FCSTD DOCUMENT  (FreeCAD 0.19R16699 (Git))
Label: RD701F Series
License: All rights reserved
LicenseURL: http://en.wikipedia.org/wiki/All_rights_reserved
objects: Sketcher::SketchObject×1, PartDesign::Body×1
note: 2 computed .brp shape members not serialized (recipe doc carries the construction recipe); baked Part::Feature solids carry a one-line shape summary decoded from their .brp

FEATURE [Sketcher::SketchObject] Sketch  label="MasterSketch"
  MapMode = 5
  Support = -> [XY_Plane]
  expr: Constraints[65] = MasterSketch.Constraints.antirotationtabdepth
  expr: Constraints.bodydepthtotal = MasterSketch.Constraints.bodyreardepth + MasterSketch.Constraints.bodyfrontdepth
  sketch-geometry (26):
    g0: LineSegment StartX=-3.85 StartY=3.85 StartZ=0 EndX=3.85 EndY=3.85 EndZ=0
    g1: LineSegment StartX=3.85 StartY=3.85 StartZ=0 EndX=3.85 EndY=-5.5 EndZ=0
    g2: LineSegment StartX=3.85 StartY=-5.5 StartZ=0 EndX=-3.85 EndY=-5.5 EndZ=0
    g3: LineSegment StartX=-3.85 StartY=-5.5 StartZ=0 EndX=-3.85 EndY=3.85 EndZ=0
    g4: GeomPoint X=-3.85 Y=0 Z=0
    g5: GeomPoint X=3.85 Y=0 Z=0
    g6: LineSegment StartX=-13.2904 StartY=12.005 StartZ=0 EndX=-14.7904 EndY=12.005 EndZ=0
    g7: LineSegment StartX=-14.7904 StartY=12.005 StartZ=0 EndX=-14.7904 EndY=2.65497 EndZ=0
    g8: LineSegment StartX=-14.7904 StartY=2.65497 StartZ=0 EndX=-13.2904 EndY=2.65497 EndZ=0
    g9: LineSegment StartX=-13.2904 StartY=2.65497 StartZ=0 EndX=-13.2904 EndY=12.005 EndZ=0
    g10: LineSegment StartX=-14.7904 StartY=2.65497 StartZ=0 EndX=-17.7904 EndY=2.65497 EndZ=0
    g11: LineSegment StartX=-17.7904 StartY=2.65497 StartZ=0 EndX=-17.7904 EndY=12.005 EndZ=0
    g12: LineSegment StartX=-17.7904 StartY=12.005 StartZ=0 EndX=-14.7904 EndY=12.005 EndZ=0
    g13: LineSegment StartX=-14.7904 StartY=12.005 StartZ=0 EndX=-14.7904 EndY=2.65497 EndZ=0
    g14: LineSegment StartX=-17.7904 StartY=12.005 StartZ=0 EndX=-18.5904 EndY=12.005 EndZ=0
    g15: LineSegment StartX=-18.5904 StartY=12.005 StartZ=0 EndX=-18.5904 EndY=2.65497 EndZ=0
    g16: LineSegment StartX=-18.5904 StartY=2.65497 StartZ=0 EndX=-17.7904 EndY=2.65497 EndZ=0
    g17: LineSegment StartX=-17.7904 StartY=2.65497 StartZ=0 EndX=-17.7904 EndY=12.005 EndZ=0
    g18: LineSegment StartX=-18.5904 StartY=2.65497 StartZ=0 EndX=-19.3904 EndY=2.65497 EndZ=0
    g19: LineSegment StartX=-19.3904 StartY=2.65497 StartZ=0 EndX=-19.3904 EndY=3.45497 EndZ=0
    g20: LineSegment StartX=-19.3904 StartY=3.45497 StartZ=0 EndX=-18.5904 EndY=3.45497 EndZ=0
    g21: LineSegment StartX=-18.5904 StartY=3.45497 StartZ=0 EndX=-18.5904 EndY=2.65497 EndZ=0
    g22: LineSegment StartX=-1 StartY=-5.5 StartZ=0 EndX=1 EndY=-5.5 EndZ=0
    g23: LineSegment StartX=1 StartY=-5.5 StartZ=0 EndX=1 EndY=-4.7 EndZ=0
    g24: LineSegment StartX=1 StartY=-4.7 StartZ=0 EndX=-1 EndY=-4.7 EndZ=0
    g25: LineSegment StartX=-1 StartY=-4.7 StartZ=0 EndX=-1 EndY=-5.5 EndZ=0
  constraints (67):
    c: Coincident(g0,g1)
    c: Coincident(g1,g2)
    c: Coincident(g2,g3)
    c: Coincident(g3,g0)
    c: Horizontal(g2)
    c: Vertical(g1)
    c: Vertical(g3)
    c: PointOnObject(g4,g3)
    c: PointOnObject(g5,g1)
    c: PointOnObject(g5,g-1)
    c: PointOnObject(g4,g-1)
    c: DistanceY(g5,g0) = 3.85  'bodyreardepth'
    c: DistanceY(g1,g5) = 5.5  'bodyfrontdepth'
    c: DistanceX(g0,g0) = 7.7  'bodywidth'
    c: Symmetric(g0,g0,g-2)
    c: Coincident(g6,g7)
    c: Coincident(g7,g8)
    c: Coincident(g8,g9)
    c: Coincident(g9,g6)
    c: Horizontal(g6)
    c: Horizontal(g8)
    c: Vertical(g7)
    c: Vertical(g9)
    c: Coincident(g10,g11)
    c: Coincident(g11,g12)
    c: Coincident(g12,g13)
    c: Coincident(g13,g10)
    c: Horizontal(g10)
    c: Horizontal(g12)
    c: Vertical(g11)
    c: Coincident(g10,g7)
    c: Coincident(g14,g15)
    c: Coincident(g15,g16)
    c: Coincident(g16,g17)
    c: Coincident(g17,g14)
    c: Horizontal(g14)
    c: Horizontal(g16)
    c: Vertical(g15)
    c: Coincident(g14,g11)
    c: Coincident(g16,g10)
    c: Coincident(g6,g12)
    c: DistanceX(g14,g6) = 5.3
    c: DistanceY(g9,g9) = 9.35  'bodydepthtotal'
    c: DistanceX(g7,g8) = 1.5  'bodybottompadlength'
    c: DistanceX(g10,g10) = 3  'bodymidpadlength'
    c: Coincident(g18,g19)
    c: Coincident(g19,g20)
    c: Coincident(g20,g21)
    c: Coincident(g21,g18)
    c: Horizontal(g18)
    c: Horizontal(g20)
    c: Vertical(g19)
    c: Vertical(g21)
    c: Coincident(g18,g15)
    c: DistanceX(g18,g18) = 0.8  'antirotationtabheight'
    c: DistanceY(g19,g19) = 0.8  'antirotationtabdepth'
    c: Coincident(g22,g23)
    c: Coincident(g23,g24)
    c: Coincident(g24,g25)
    c: Coincident(g25,g22)
    c: Horizontal(g22)
    c: Vertical(g23)
    c: Vertical(g25)
    c: PointOnObject(g22,g2)
    c: DistanceX(g24,g24) = 2  'antirotationtabwidth'
    c: DistanceY(g23,g23) = 0.8
    c: Symmetric(g23,g24,g-2)
FEATURE [PartDesign::Body] Body  label="MasterSketchBody"
  Group = -> [Sketch]
  Origin = -> Origin
